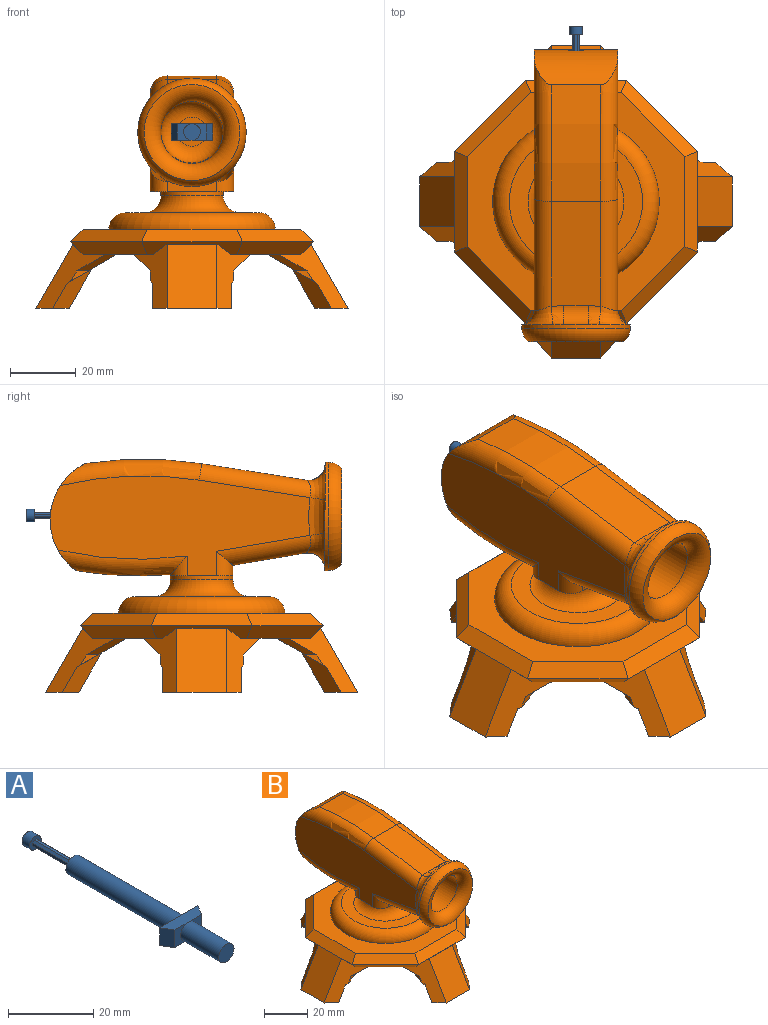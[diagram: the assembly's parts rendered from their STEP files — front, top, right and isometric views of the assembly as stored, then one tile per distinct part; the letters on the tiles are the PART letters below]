
ASSEMBLY  parts=2 mates=1
PART A: 23 faces, bbox 12.7x66x5.1 mm
  f0: plane 5.08x4.52mm, normal (0,-1,0), area 12.8mm2, adj f15,f16,f17,f21
  f1: cylinder r=2.54mm len=34.93mm, axis (0,1,0), area 557.4mm2, adj f2,f14,f18
  f2: plane 5.08x5.08mm, normal (0,1,0), area 17.4mm2, adj f1,f3,f4,f5,f6,f7,f8,f9
  f3: plane 12.7x0.78mm, normal (0,0,1), area 9.9mm2, adj f2,f4,f10,f13
  f4: plane 12.7x0.55mm, normal (0.71,0,0.71), area 9.9mm2, adj f2,f3,f5,f13
  f5: plane 12.7x0.78mm, normal (1,0,0), area 9.9mm2, adj f2,f4,f6,f13
  f6: plane 12.7x0.55mm, normal (0.71,0,-0.71), area 9.9mm2, adj f2,f5,f7,f13
  f7: plane 12.7x0.78mm, normal (0,0,-1), area 9.9mm2, adj f2,f6,f8,f13
  f8: plane 12.7x0.55mm, normal (-0.71,0,-0.71), area 9.9mm2, adj f2,f7,f9,f13
  f9: plane 12.7x0.78mm, normal (-1,0,0), area 9.9mm2, adj f2,f8,f10,f13
  f10: plane 12.7x0.55mm, normal (-0.71,0,0.71), area 9.9mm2, adj f2,f3,f9,f13
  f11: cylinder r=1.91mm len=3.81mm, axis (0,-1,0), area 30.4mm2, adj f12,f13
  f12: plane 3.81x3.81mm, normal (0,1,0), area 11.4mm2, adj f11
  f13: plane 3.81x3.81mm, normal (0,-1,0), area 8.5mm2, adj f3,f4,f5,f6,f7,f8,f9,f10
  f14: plane 6.35x5.08mm, normal (0,1,0), area 22.1mm2, adj f1,f15,f16,f17
  f15: plane 12.7x3.18mm, normal (0,0,1), area 34.5mm2, adj f0,f14,f17,f18,f19,f20
  f16: plane 12.7x3.18mm, normal (0,0,-1), area 34.5mm2, adj f0,f14,f17,f18,f19,f20
  f17: plane 5.08x3.18mm, normal (0.87,-0.5,0), area 18.6mm2, adj f0,f14,f15,f16
  f18: plane 6.35x5.08mm, normal (0,1,0), area 22.1mm2, adj f1,f15,f16,f19
  f19: plane 5.08x3.18mm, normal (-0.87,-0.5,0), area 18.6mm2, adj f15,f16,f18,f20
  f20: plane 5.08x4.52mm, normal (0,-1,0), area 12.8mm2, adj f15,f16,f19,f21
  f21: cylinder r=2.54mm len=12.7mm, axis (0,1,0), area 202.7mm2, adj f0,f20,f22
  f22: plane 5.08x5.08mm, normal (0,-1,0), area 20.3mm2, adj f21
PART B: 114 faces, bbox 95.3x95.3x73.4 mm
  f0: plane 66.45x66.45mm, normal (0,0,-1), area 2346.4mm2, adj f51,f57,f63,f69,f72,f74,f76,f78
  f1: plane 7.48x0.43mm, normal (0,1,0), area 2.1mm2, adj f16,f32
  f2: cylinder r=9.53mm len=19.05mm, axis (0,0,-1), area 75.7mm2, adj f5,f6,f7,f70
  f3: plane 66.45x66.45mm, normal (0,0,1), area 1630.9mm2, adj f71,f88,f89,f90,f91,f92,f93,f94
  f4: plane 40.64x40.64mm, normal (0,0,1), area 627.1mm2, adj f70,f71
  f5: plane 19.05x9.53mm, normal (0,0,1), area 142.5mm2, adj f2,f7
  f6: plane 15.24x0.38mm, normal (0,1,0), area 5.8mm2, adj f2,f7,f8,f39,f41
  f7: plane 25.41x19.06mm, normal (0,0,-1), area 319.3mm2, adj f2,f5,f6,f13,f14,f15,f38,f39
  f8: cylinder r=114.3mm len=28.72mm, axis (-1,0,0), area 439.2mm2, adj f6,f9,f23,f25
  f9: cylinder r=19.05mm len=32.62mm, axis (-1,0,0), area 930.4mm2, adj f8,f10,f14,f15,f18,f21,f23,f25
  f10: cylinder r=114.3mm len=35.56mm, axis (-1,0,0), area 544.1mm2, adj f9,f11,f18,f21
  f11: plane 31.95x15.25mm, normal (0,-0.16,0.99), area 490.8mm2, adj f10,f19,f20,f30,f32,f34
  f12: plane 22.27x15.25mm, normal (0,-0.17,-0.99), area 341.8mm2, adj f13,f22,f24,f29,f31,f33
  f13: plane 15.24x3.17mm, normal (0,-1,0), area 48.3mm2, adj f7,f12,f38,f40
  f14: plane 79.26x30.51mm, normal (1,0,0), area 1692mm2, adj f7,f9,f20,f21,f24,f25,f37,f40
  f15: plane 79.26x30.51mm, normal (-1,0,0), area 1692mm2, adj f7,f9,f18,f19,f22,f23,f26,f38
  f16: cylinder r=16.51mm len=33.02mm, axis (0,1,0), area 115.6mm2, adj f1,f17,f26,f27,f28,f29,f30,f33
  f17: plane 6.4x0.31mm, normal (0,1,0), area 1.3mm2, adj f16,f31
  f18: torus R=109.22mm, axis (1,0,0), area 310.5mm2, adj f9,f10,f15,f19
  f19: cylinder r=5.08mm len=34.61mm, axis (0,-0.99,-0.16), area 265.6mm2, adj f11,f15,f18,f28
  f20: cylinder r=5.08mm len=34.61mm, axis (0,0.99,0.16), area 265.6mm2, adj f11,f14,f21,f36
  f21: torus R=109.22mm, axis (1,0,0), area 310.5mm2, adj f9,f10,f14,f20
  f22: cylinder r=5.08mm len=29.4mm, axis (0,0.99,-0.17), area 201mm2, adj f12,f15,f27,f38
  f23: torus R=109.22mm, axis (1,0,0), area 264.7mm2, adj f8,f9,f15,f39
  f24: cylinder r=5.08mm len=29.4mm, axis (0,-0.99,0.17), area 201mm2, adj f12,f14,f35,f40
  f25: torus R=109.22mm, axis (1,0,0), area 264.7mm2, adj f8,f9,f14,f41
  f26: bspline ~11.53x4.94mm, area 68.9mm2, adj f15,f16,f27,f28
  f27: bspline ~11.4x9.76mm, area 56.7mm2, adj f16,f22,f26,f29
  f28: bspline ~11.43x9.74mm, area 56.6mm2, adj f16,f19,f26,f30
  f29: bspline ~6.14x6.05mm, area 33.6mm2, adj f12,f16,f27,f31
  f30: bspline ~6.16x6.15mm, area 29.1mm2, adj f11,f16,f28,f32
  f31: cylinder r=5.08mm len=6.4mm, axis (-1,0,0), area 56.7mm2, adj f12,f17,f29,f33
  f32: cylinder r=5.08mm len=7.48mm, axis (1,0,0), area 65.5mm2, adj f1,f11,f30,f34
  f33: bspline ~6.89x6.21mm, area 33.6mm2, adj f12,f16,f31,f35
  f34: bspline ~6.16x6.15mm, area 29.1mm2, adj f11,f16,f32,f36
  f35: bspline ~11.4x9.76mm, area 56.7mm2, adj f16,f24,f33,f37
  f36: bspline ~11.43x9.74mm, area 56.6mm2, adj f16,f20,f34,f37
  f37: bspline ~11.53x4.94mm, area 68.9mm2, adj f14,f16,f35,f36
  f38: cylinder r=5.08mm len=7.47mm, axis (0,0,-1), area 37.8mm2, adj f7,f13,f15,f22
  f39: cylinder r=5.08mm len=6.05mm, axis (0,0,1), area 19.3mm2, adj f6,f7,f15,f23
  f40: cylinder r=5.08mm len=7.47mm, axis (0,0,1), area 37.8mm2, adj f7,f13,f14,f24
  f41: cylinder r=5.08mm len=6.05mm, axis (0,0,-1), area 19.3mm2, adj f6,f7,f14,f25
  f42: cylinder r=9.53mm len=53.41mm, axis (0,-1,0), area 3192.3mm2, adj f44,f45
  f43: plane 8.89x8.89mm, normal (0,-1,0), area 41.8mm2, adj f45,f113
  f44: torus R=14.61mm, axis (0,-1,0), area 570.1mm2, adj f42,f112
  f45: torus R=4.45mm, axis (0,-1,0), area 385mm2, adj f42,f43
  f46: plane 15.24x12.1mm, normal (-0.87,0,-0.5), area 212.9mm2, adj f47,f51,f84,f86
  f47: plane 24.04x10.16mm, normal (0,0,-1), area 199.5mm2, adj f46,f48,f84,f85,f86,f87
  f48: plane 19.59x15.24mm, normal (0.87,0,0.5), area 344.7mm2, adj f47,f85,f87,f96
  f49: plane 5.26x3.04mm, normal (0,-1,0), area 5.3mm2, adj f51,f85,f104
  f50: plane 5.26x3.04mm, normal (0,1,0), area 5.3mm2, adj f51,f87,f105
  f51: plane 35.56x15.24mm, normal (-0.5,0,-0.87), area 324.9mm2, adj f0,f46,f49,f50,f84,f85,f86,f87
  f52: plane 15.24x12.1mm, normal (0.87,0,-0.5), area 212.9mm2, adj f54,f57,f77,f79
  f53: plane 19.59x15.24mm, normal (-0.87,0,0.5), area 344.7mm2, adj f54,f76,f78,f103
  f54: plane 24.04x10.16mm, normal (0,0,-1), area 199.5mm2, adj f52,f53,f76,f77,f78,f79
  f55: plane 5.26x3.04mm, normal (0,-1,0), area 5.3mm2, adj f57,f76,f108
  f56: plane 5.26x3.04mm, normal (0,1,0), area 5.3mm2, adj f57,f78,f109
  f57: plane 35.56x15.24mm, normal (0.5,0,-0.87), area 324.9mm2, adj f0,f52,f55,f56,f76,f77,f78,f79
  f58: plane 15.24x12.1mm, normal (0,-0.87,-0.5), area 212.9mm2, adj f59,f63,f73,f75
  f59: plane 24.04x10.16mm, normal (0,0,-1), area 199.5mm2, adj f58,f60,f72,f73,f74,f75
  f60: plane 19.59x15.24mm, normal (0,0.87,0.5), area 344.7mm2, adj f59,f72,f74,f100
  f61: plane 5.26x3.04mm, normal (1,0,0), area 5.3mm2, adj f63,f74,f111
  f62: plane 5.26x3.04mm, normal (-1,0,0), area 5.3mm2, adj f63,f72,f110
  f63: plane 35.56x15.24mm, normal (0,-0.5,-0.87), area 324.9mm2, adj f0,f58,f61,f62,f72,f73,f74,f75
  f64: plane 15.24x12.1mm, normal (0,0.87,-0.5), area 212.9mm2, adj f66,f69,f80,f83
  f65: plane 19.59x15.24mm, normal (0,-0.87,0.5), area 344.7mm2, adj f66,f81,f82,f99
  f66: plane 24.04x10.16mm, normal (0,0,-1), area 199.5mm2, adj f64,f65,f80,f81,f82,f83
  f67: plane 5.26x3.04mm, normal (1,0,0), area 5.3mm2, adj f69,f82,f106
  f68: plane 5.26x3.04mm, normal (-1,0,0), area 5.3mm2, adj f69,f81,f107
  f69: plane 35.56x15.24mm, normal (0,0.5,-0.87), area 324.9mm2, adj f0,f64,f67,f68,f80,f81,f82,f83
  f70: torus R=14.61mm, axis (0,0,1), area 570.1mm2, adj f2,f4
  f71: torus R=20.32mm, axis (0,0,1), area 1180.9mm2, adj f3,f4
  f72: plane 21.26x19.59mm, normal (-0.71,0.61,0.35), area 159.7mm2, adj f0,f59,f60,f62,f63,f73,f100,f110
  f73: plane 12.1x12.07mm, normal (-0.71,-0.61,-0.35), area 71.1mm2, adj f58,f59,f63,f72
  f74: plane 21.26x19.59mm, normal (0.71,0.61,0.35), area 159.7mm2, adj f0,f59,f60,f61,f63,f75,f100,f111
  f75: plane 12.1x12.07mm, normal (0.71,-0.61,-0.35), area 71.1mm2, adj f58,f59,f63,f74
  f76: plane 21.26x19.59mm, normal (-0.61,-0.71,0.35), area 159.7mm2, adj f0,f53,f54,f55,f57,f77,f103,f108
  f77: plane 12.1x12.07mm, normal (0.61,-0.71,-0.35), area 71.1mm2, adj f52,f54,f57,f76
  f78: plane 21.26x19.59mm, normal (-0.61,0.71,0.35), area 159.7mm2, adj f0,f53,f54,f56,f57,f79,f103,f109
  f79: plane 12.1x12.07mm, normal (0.61,0.71,-0.35), area 71.1mm2, adj f52,f54,f57,f78
  f80: plane 12.1x12.07mm, normal (-0.71,0.61,-0.35), area 71.1mm2, adj f64,f66,f69,f81
  f81: plane 21.26x19.59mm, normal (-0.71,-0.61,0.35), area 159.7mm2, adj f0,f65,f66,f68,f69,f80,f99,f107
  f82: plane 21.26x19.59mm, normal (0.71,-0.61,0.35), area 159.7mm2, adj f0,f65,f66,f67,f69,f83,f99,f106
  f83: plane 12.1x12.07mm, normal (0.71,0.61,-0.35), area 71.1mm2, adj f64,f66,f69,f82
  f84: plane 12.1x12.07mm, normal (-0.61,-0.71,-0.35), area 71.1mm2, adj f46,f47,f51,f85
  f85: plane 21.26x19.59mm, normal (0.61,-0.71,0.35), area 159.7mm2, adj f0,f47,f48,f49,f51,f84,f96,f104
  f86: plane 12.1x12.07mm, normal (-0.61,0.71,-0.35), area 71.1mm2, adj f46,f47,f51,f87
  f87: plane 21.26x19.59mm, normal (0.61,0.71,0.35), area 159.7mm2, adj f0,f47,f48,f50,f51,f86,f96,f105
  f88: plane 30.68x3.81mm, normal (0,-0.71,0.71), area 156.8mm2, adj f3,f89,f90,f99
  f89: plane 23.27x23.27mm, normal (-0.5,-0.5,0.71), area 156.8mm2, adj f3,f88,f91,f101
  f90: plane 23.27x23.27mm, normal (0.5,-0.5,0.71), area 156.8mm2, adj f3,f88,f92,f97
  f91: plane 30.68x3.81mm, normal (-0.71,0,0.71), area 156.8mm2, adj f3,f89,f93,f103
  f92: plane 30.68x3.81mm, normal (0.71,0,0.71), area 156.8mm2, adj f3,f90,f94,f96
  f93: plane 23.27x23.27mm, normal (-0.5,0.5,0.71), area 156.8mm2, adj f3,f91,f95,f102
  f94: plane 23.27x23.27mm, normal (0.5,0.5,0.71), area 156.8mm2, adj f3,f92,f95,f98
  f95: plane 30.68x3.81mm, normal (0,0.71,0.71), area 156.8mm2, adj f3,f93,f94,f100
  f96: plane 30.68x3.81mm, normal (0.71,0,-0.71), area 71.7mm2, adj f0,f48,f85,f87,f92,f97,f98
  f97: plane 23.27x23.27mm, normal (0.5,-0.5,-0.71), area 156.8mm2, adj f0,f90,f96,f99
  f98: plane 23.27x23.27mm, normal (0.5,0.5,-0.71), area 156.8mm2, adj f0,f94,f96,f100
  f99: plane 30.68x3.81mm, normal (0,-0.71,-0.71), area 71.7mm2, adj f0,f65,f81,f82,f88,f97,f101
  f100: plane 30.68x3.81mm, normal (0,0.71,-0.71), area 71.7mm2, adj f0,f60,f72,f74,f95,f98,f102
  f101: plane 23.27x23.27mm, normal (-0.5,-0.5,-0.71), area 156.8mm2, adj f0,f89,f99,f103
  f102: plane 23.27x23.27mm, normal (-0.5,0.5,-0.71), area 156.8mm2, adj f0,f93,f100,f103
  f103: plane 30.68x3.81mm, normal (-0.71,0,-0.71), area 71.7mm2, adj f0,f53,f76,f78,f91,f101,f102
  f104: plane 12.31x5.08mm, normal (0,-0.71,-0.71), area 25.2mm2, adj f0,f49,f51,f85
  f105: plane 12.31x5.08mm, normal (0,0.71,-0.71), area 25.2mm2, adj f0,f50,f51,f87
  f106: plane 12.31x5.08mm, normal (0.71,0,-0.71), area 25.2mm2, adj f0,f67,f69,f82
  f107: plane 12.31x5.08mm, normal (-0.71,0,-0.71), area 25.2mm2, adj f0,f68,f69,f81
  f108: plane 12.31x5.08mm, normal (0,-0.71,-0.71), area 25.2mm2, adj f0,f55,f57,f76
  f109: plane 12.31x5.08mm, normal (0,0.71,-0.71), area 25.2mm2, adj f0,f56,f57,f78
  f110: plane 12.31x5.08mm, normal (-0.71,0,-0.71), area 25.2mm2, adj f0,f62,f63,f72
  f111: plane 12.31x5.08mm, normal (0.71,0,-0.71), area 25.2mm2, adj f0,f61,f63,f74
  f112: torus R=11.43mm, axis (0,-1,0), area 453.3mm2, adj f16,f44
  f113: cylinder r=2.54mm len=25.38mm, axis (0,-1,0), area 404.8mm2, adj f9,f43
PLACE A rot(axis=(1,0,0),0.2deg) t=(-175.58,120.96,25.14)mm
PLACE B t=(-175.58,82.68,-12.28)mm
MATE slider A.f1 <-> B.f113  axis (0,1,0) through (-175.58,103.5,25.08)mm
